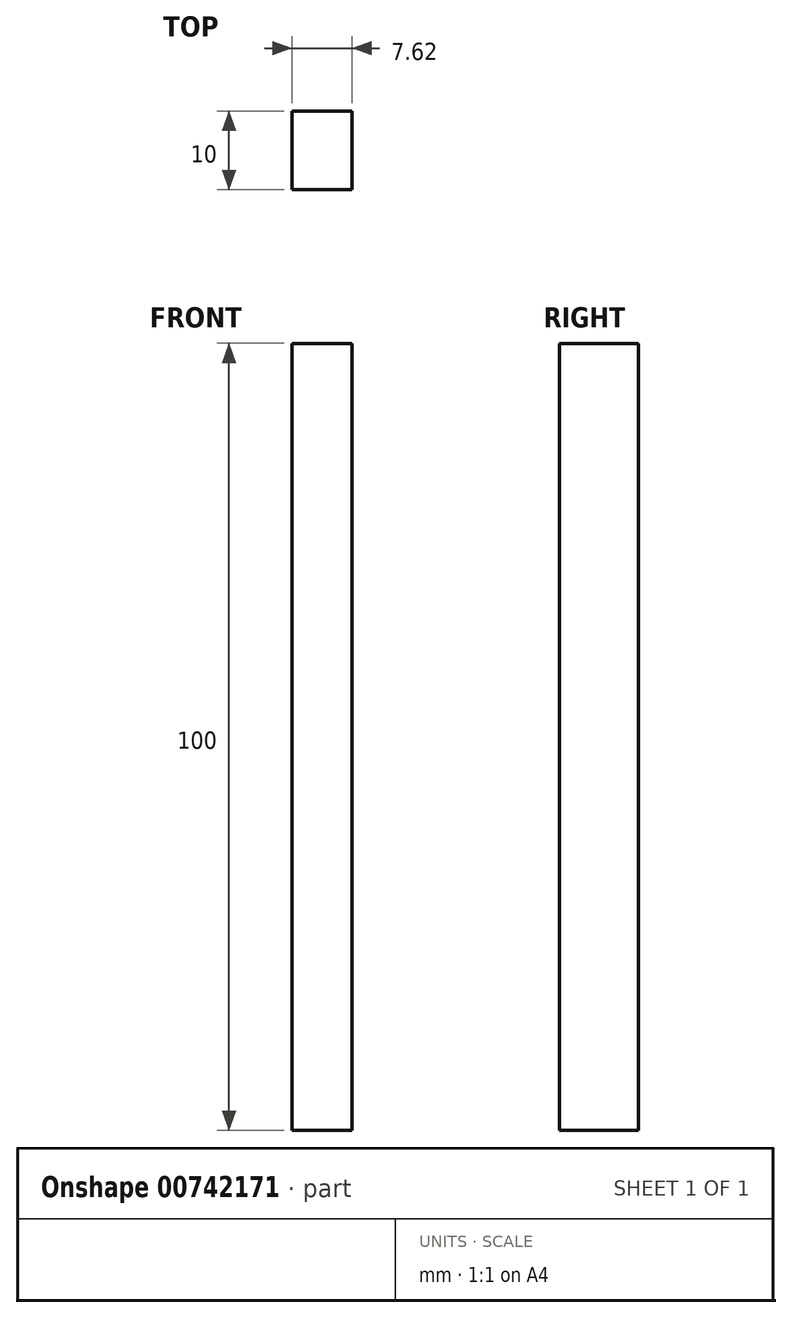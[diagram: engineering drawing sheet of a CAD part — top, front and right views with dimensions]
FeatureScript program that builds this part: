
annotation { "Feature Type Name" : "Feature", "Feature Type Description" : "" }
export const myFeature = defineFeature(function(context is Context, id is Id, definition is map)
    precondition{}
    {
        {
            var Q0;
            Q0=qCreatedBy(makeId("Front.planeOp"),FACE);
            var sketch = newSketch(context, id + "F0", { "sketchPlane" : qUnion([Q0])});
            skLineSegment(sketch, "E0.bottom", {"start": v(-7.62, 24) * mm, "end": v(0, 24) * mm});
            skLineSegment(sketch, "E0.top", {"start": v(-7.62, -76) * mm, "end": v(0, -76) * mm});
            skLineSegment(sketch, "E0.left", {"start": v(-7.62, 24) * mm, "end": v(-7.62, -76) * mm});
            skLineSegment(sketch, "E0.right", {"start": v(0, 24) * mm, "end": v(0, -76) * mm});
            skSolve(sketch);
        }
        {
            var Q0;
            Q0=makeQuery(id+"F0.imprint","IMPRINT",FACE,{"disambiguationData":[TD([[makeQuery(id+"F0.imprint","IMPRINT",EDGE,{"derivedFrom":sQuery(id+"F0.wireOp",EDGE,"E0.bottom")}),-1.0]])]});
            extrude(context, id + "F1", {"entities" : qUnion([Q0]), "depth" : 10 * mm, "offsetDistance" : 25 * mm});
        }
    });
